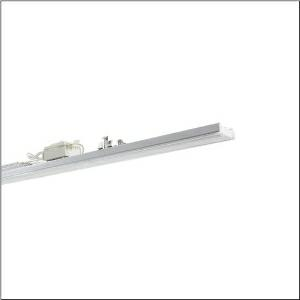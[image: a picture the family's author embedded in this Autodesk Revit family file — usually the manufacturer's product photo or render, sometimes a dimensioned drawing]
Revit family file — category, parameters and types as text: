
# Revit family: licross_r__11_recessed_mo_51te107n485g_8dc9
name_source: partatom
category: Lighting Fixtures
units: mm (PartAtom-declared; Revit-internal decimal feet)

## family parameters
Cut with Voids When Loaded = No
Host = Face
Light Source = No
Part Type = Normal
Room Calculation Point = No
Round Connector Dimension = Use Diameter
Shared = No

## types (1)
- Licross® 11 Recessed MO (1 x LED, 8700 lm, 48.5 W, 4000K)
    Apparent Load = 49 VA
    CIE Flux Codes = 50 81 96 100 100
    Color Rendering = 80
    Color Temperature = 4000K
    Default Elevation = 1800 mm
    Description = Licross® 11 Recessed MO, luminaire insert, of sheet steel, galvanised, coil coated, white, length: 1.500mm, width: 66mm, height: 67mm, LED rated luminous flux: 8.710lm, light colour: 840, control gear: ON/OFF, with plug, 3-pole, with phase selection, mains connection: 220..240V, AC, 50/60Hz, rated input power: 49W, internal wiring halogen-free, primary optical cover: cover, of PMMA, light emission: direct distribution, primary light characteristic: symmetric, protection rating (complete): IP54, insulation class (complete): insulation class I (protective earthing), certification: CE, ENEC, VDE, UKCA, protection symbol: D if used in an environment with non-conductive dust loads with corresponding accessories, impact resistance: IK06, permissible ambient temperature for indoor applications: -35..+35°C, corresponds to IFS (International Featured Standards) requirements for safety and quality in the food industry, reducing of maximum allowable ambient temperature of 5°C with ceiling mounting, packaging unit: 1 piece
    Height = 58 mm
    Lamp = 1 x LED
    Lamp Light Flux = 8700 lm
    Lamp Power = 48.5 W
    Lamp count = 1
    Length = 1500 mm
    Luminous efficacy = 179 lm/W
    Manufacturer = Siteco
    ModVariant = No
    Model = 51TE107N485G
    Mounting Place = Ceiling
    Mounting Type = Pendant
    Number of Poles = 1
    OnlyDefault = Yes
    Power Factor = 1
    Product Name = Licross® 11 Recessed MO
    Product group = luminaire insert | ceiling pendant
    ProductGroupID = 902
    Protection Class = Protection class I
    Protection Degree = IP 54
    RLX_Detail_Level = 1
    RLX_Emergency_Light_Flux = 0 lm
    RLX_Emergency_Type = 0
    RLX_Emergency_Type_DB = No
    RlxData = <blob elided: 20737 chars, md5=843a7127>
    Socket = socket
    Standby Power = 0 W
    System Light Flux = 8700 lm
    System Power = 49 W
    Type Comments = Product without accessories
    Type Image = l_1296930.jpg
    URL = http://relux.com
    VarID = ---
    Voltage = 0 V
    Weight = 0.00 kg
    Width = 66 mm

## geometry (parser evidence)
native form markers: Blend x4, Sweep x11
no freeform markers — native parametric forms only
